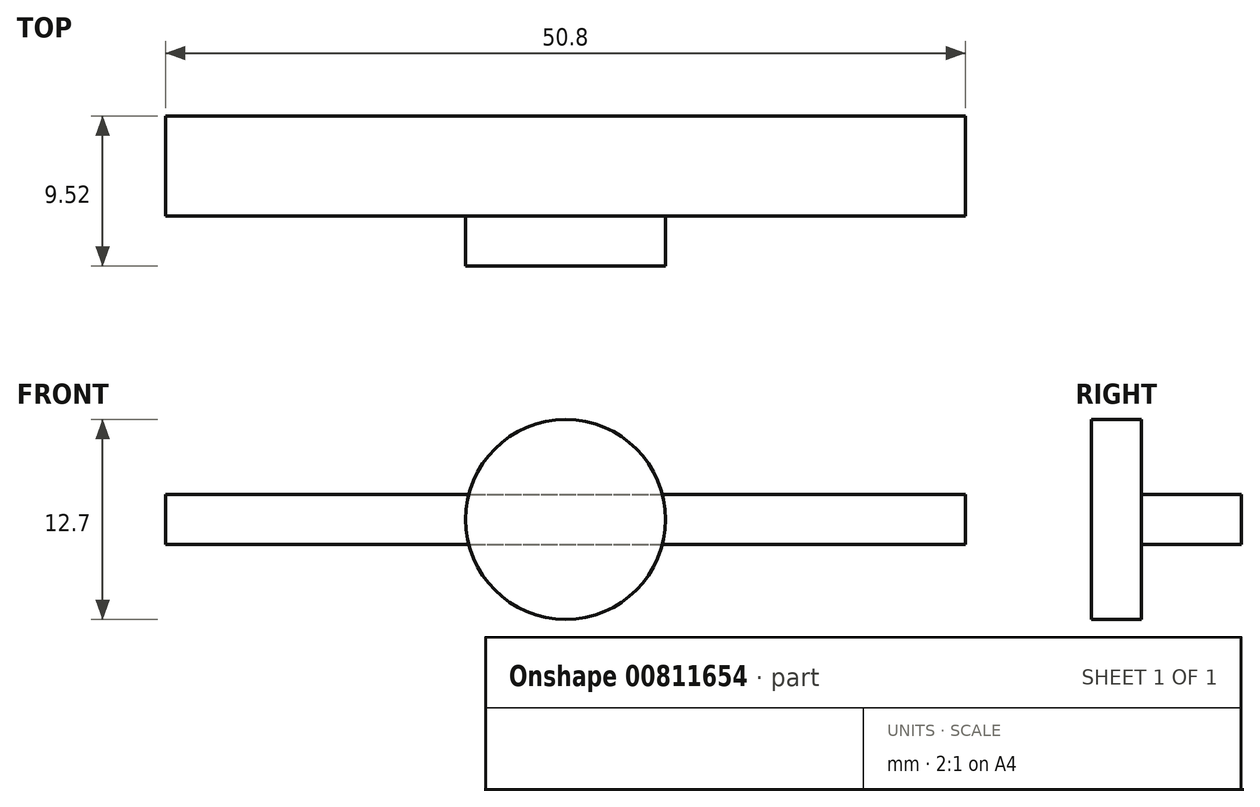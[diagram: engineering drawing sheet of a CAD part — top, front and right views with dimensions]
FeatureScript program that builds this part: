
annotation { "Feature Type Name" : "Feature", "Feature Type Description" : "" }
export const myFeature = defineFeature(function(context is Context, id is Id, definition is map)
    precondition{}
    {
        {
            var Q0;
            Q0=qCreatedBy(makeId("Top.planeOp"),FACE);
            var sketch = newSketch(context, id + "F0", { "sketchPlane" : qUnion([Q0])});
            skLineSegment(sketch, "E0.bottom", {"start": v(-8.45, 22.66) * mm, "end": v(4.25, 22.66) * mm});
            skLineSegment(sketch, "E0.top", {"start": v(-8.45, 19.49) * mm, "end": v(4.25, 19.49) * mm});
            skLineSegment(sketch, "E0.left", {"start": v(-8.45, 22.66) * mm, "end": v(-8.45, 19.49) * mm});
            skLineSegment(sketch, "E0.right", {"start": v(4.25, 22.66) * mm, "end": v(4.25, 19.49) * mm});
            skLineSegment(sketch, "E1", {"start": v(4.25, 22.66) * mm, "end": v(23.3, 22.66) * mm});
            skLineSegment(sketch, "E2", {"start": v(-8.45, 22.66) * mm, "end": v(-27.5, 22.66) * mm});
            skLineSegment(sketch, "E3", {"start": v(-27.5, 22.66) * mm, "end": v(-27.5, 29.01) * mm});
            skLineSegment(sketch, "E4", {"start": v(-27.5, 29.01) * mm, "end": v(23.3, 29.01) * mm});
            skLineSegment(sketch, "E5", {"start": v(23.3, 29.01) * mm, "end": v(23.3, 22.66) * mm});
            skLineSegment(sketch, "E6", {"start": v(-24.32, 29.01) * mm, "end": v(-11.62, 29.01) * mm});
            skLineSegment(sketch, "E7", {"start": v(-8.45, 29.01) * mm, "end": v(-2.1, 29.01) * mm});
            skLineSegment(sketch, "E8", {"start": v(-2.1, 29.01) * mm, "end": v(4.25, 29.01) * mm});
            skLineSegment(sketch, "E9", {"start": v(-2.1, 22.66) * mm, "end": v(-2.1, 19.49) * mm});
            skSolve(sketch);
        }
        {
            var Q0;
            {var subQ0=sQuery(id+"F0.wireOp",EDGE,"E0.left");Q0=makeQuery(id+"F0.imprint","IMPRINT",FACE,{"disambiguationData":[TD([[makeQuery(id+"F0.imprint","IMPRINT",EDGE,{"derivedFrom":subQ0}),1.0]])]});}
            var Q1;
            Q1=sQuery(id+"F0.wireOp",EDGE,"E9");
            revolve(context, id + "F1", {"surfaceOperationType" : NewSurfaceOperationType.NEW, "entities" : qUnion([Q0]), "axis" : qUnion([Q1]), "revolveType" : RevolveType.FULL});
        }
        {
            var Q0;
            {var subQ9=sQuery(id+"F0.wireOp",EDGE,"E1");Q0=makeQuery(id+"F0.imprint","IMPRINT",FACE,{"disambiguationData":[TD([[makeQuery(id+"F0.imprint","IMPRINT",EDGE,{"derivedFrom":subQ9}),1.0]])]});}
            extrude(context, id + "F2", {"entities" : qUnion([Q0]), "operationType" : NewBodyOperationType.ADD, "endBound" : BoundingType.SYMMETRIC, "depth" : 3.17 * mm, "offsetDistance" : 25.4 * mm});
        }
    });
